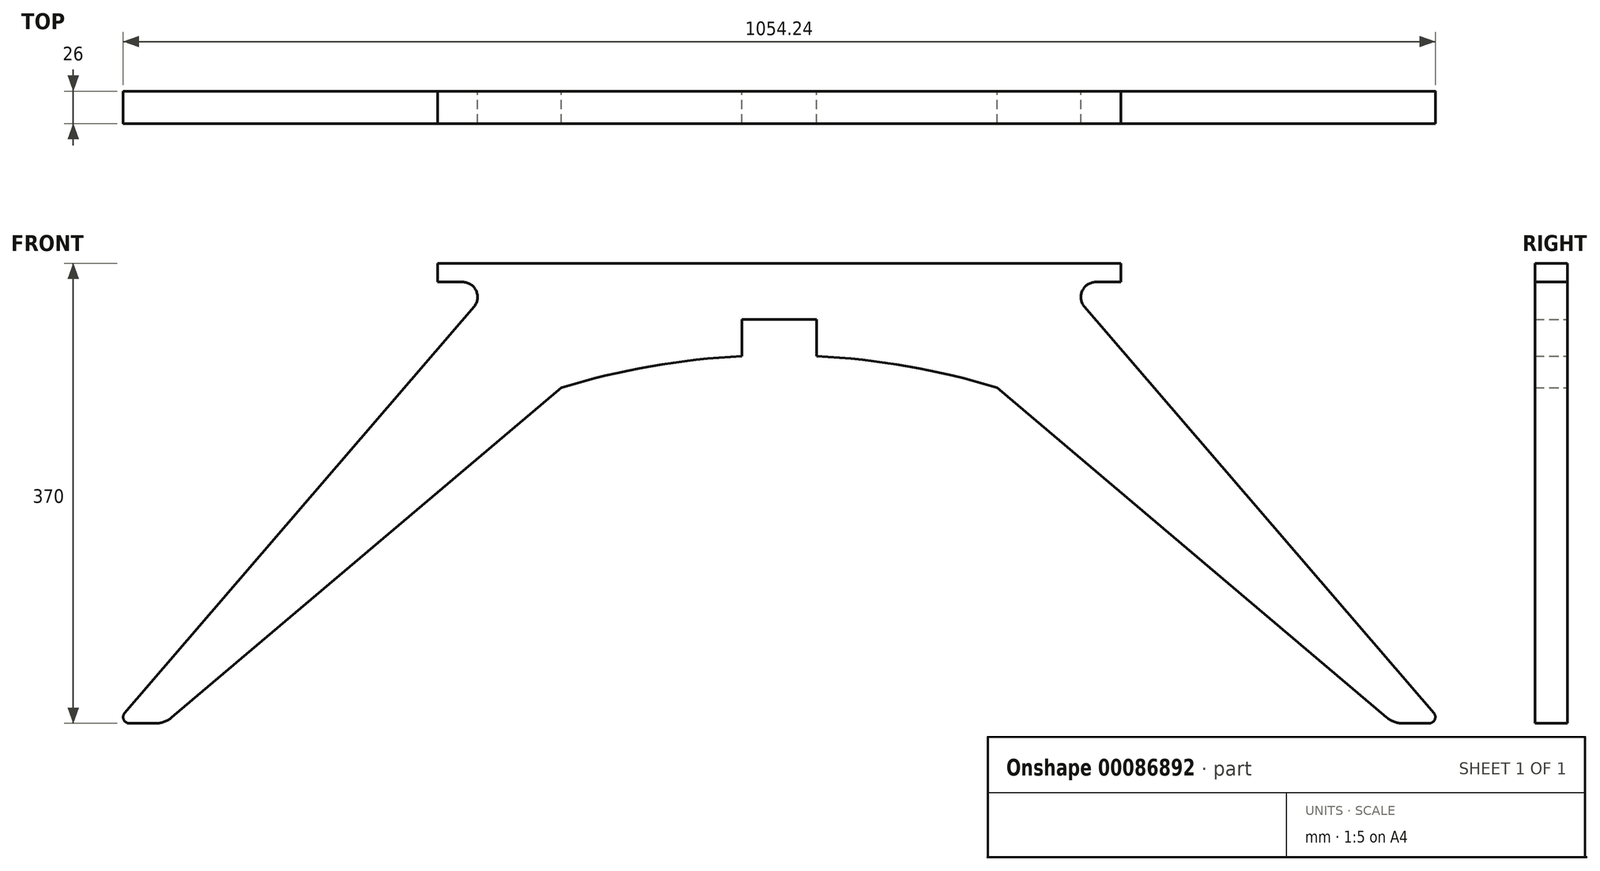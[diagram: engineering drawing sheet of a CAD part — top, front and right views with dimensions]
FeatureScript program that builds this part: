
annotation { "Feature Type Name" : "Feature", "Feature Type Description" : "" }
export const myFeature = defineFeature(function(context is Context, id is Id, definition is map)
    precondition{}
    {
        {
            var Q0;
            Q0=qCreatedBy(makeId("Front.planeOp"),FACE);
            var sketch = newSketch(context, id + "F0", { "sketchPlane" : qUnion([Q0])});
            skLineSegment(sketch, "E0", {"start": v(525.9, -361.74) * mm, "end": v(245.31, -35) * mm});
            skLineSegment(sketch, "E1", {"start": v(522.12, -370) * mm, "end": v(500.93, -370) * mm});
            skLineSegment(sketch, "E2", {"start": v(533, 383.5) * mm, "end": v(533, -561.05) * mm, "construction": true});
            skPoint(sketch, "E3.visualSharp", {"position": v(533, -370) * mm});
            skArc(sketch, "E3.filletArc", {"start": v(522.12, -370) * mm, "mid": v(526.66, -367.09) * mm, "end": v(525.9, -361.74) * mm});
            skArc(sketch, "E4", {"start": v(500.93, -370) * mm, "mid": v(494.04, -368.78) * mm, "end": v(488, -365.26) * mm});
            skPoint(sketch, "E5.orphan", {"position": v(493, -370) * mm});
            skLineSegment(sketch, "E6", {"start": v(-533, 568.71) * mm, "end": v(-533, -664.54) * mm, "construction": true});
            skLineSegment(sketch, "E7", {"start": v(0, -665.77) * mm, "end": v(0, 567.49) * mm, "construction": true});
            skArc(sketch, "E8.MirrorCS", {"start": v(-522.12, -370) * mm, "mid": v(-526.66, -367.09) * mm, "end": v(-525.9, -361.74) * mm});
            skLineSegment(sketch, "E9.MirrorCS", {"start": v(-522.12, -370) * mm, "end": v(-500.93, -370) * mm});
            skArc(sketch, "E10.MirrorCS", {"start": v(-500.93, -370) * mm, "mid": v(-494.04, -368.78) * mm, "end": v(-488, -365.26) * mm});
            skPoint(sketch, "E11.MirrorP", {"position": v(-493, -370) * mm});
            skLineSegment(sketch, "E12.MirrorCS", {"start": v(-525.9, -361.74) * mm, "end": v(-245.31, -35) * mm});
            skPoint(sketch, "E13.MirrorP", {"position": v(-533, -370) * mm});
            skLineSegment(sketch, "E14", {"start": v(488, -365.26) * mm, "end": v(175, -100) * mm});
            skLineSegment(sketch, "E15", {"start": v(-488, -365.26) * mm, "end": v(-175, -100) * mm});
            skLineSegment(sketch, "E16.bottom", {"start": v(-571.7, 18.68) * mm, "end": v(648.3, 18.68) * mm, "construction": true});
            skLineSegment(sketch, "E16.top", {"start": v(-571.7, -591.32) * mm, "end": v(648.3, -591.32) * mm, "construction": true});
            skLineSegment(sketch, "E16.left", {"start": v(-571.7, 18.68) * mm, "end": v(-571.7, -591.32) * mm, "construction": true});
            skLineSegment(sketch, "E16.right", {"start": v(648.3, 18.68) * mm, "end": v(648.3, -591.32) * mm, "construction": true});
            skArc(sketch, "E17", {"start": v(245.31, -35) * mm, "mid": v(243.5, -22.06) * mm, "end": v(254.5, -15) * mm});
            skLineSegment(sketch, "E18", {"start": v(254.5, -15) * mm, "end": v(274.5, -15) * mm});
            skLineSegment(sketch, "E19", {"start": v(274.5, -15) * mm, "end": v(274.5, 0) * mm});
            skLineSegment(sketch, "E20", {"start": v(274.5, 0) * mm, "end": v(-274.5, 0) * mm});
            skLineSegment(sketch, "E21", {"start": v(-274.5, 0) * mm, "end": v(-274.5, -15) * mm});
            skLineSegment(sketch, "E22", {"start": v(-274.5, -15) * mm, "end": v(-254.5, -15) * mm});
            skArc(sketch, "E23", {"start": v(-254.5, -15) * mm, "mid": v(-243.5, -22.06) * mm, "end": v(-245.31, -35) * mm});
            skPoint(sketch, "E24", {"position": v(0, 0) * mm});
            skArc(sketch, "E25", {"start": v(-175, -100) * mm, "mid": v(-103.28, -82.87) * mm, "end": v(-30, -74.66) * mm});
            skLineSegment(sketch, "E26.top", {"start": v(-30, -45) * mm, "end": v(30, -45) * mm});
            skLineSegment(sketch, "E26.left", {"start": v(-30, -74.66) * mm, "end": v(-30, -45) * mm});
            skLineSegment(sketch, "E26.right", {"start": v(30, -74.66) * mm, "end": v(30, -45) * mm});
            skPoint(sketch, "E27", {"position": v(0, -45) * mm});
            skArc(sketch, "E28.trimOffspring", {"start": v(30, -74.66) * mm, "mid": v(103.28, -82.87) * mm, "end": v(175, -100) * mm});
            skSolve(sketch);
        }
        {
            var Q0;
            Q0 = qSketchRegion(id + "F0", true);
            extrude(context, id + "F1", {"entities" : qUnion([Q0]), "depth" : 26 * mm});
        }
    });
